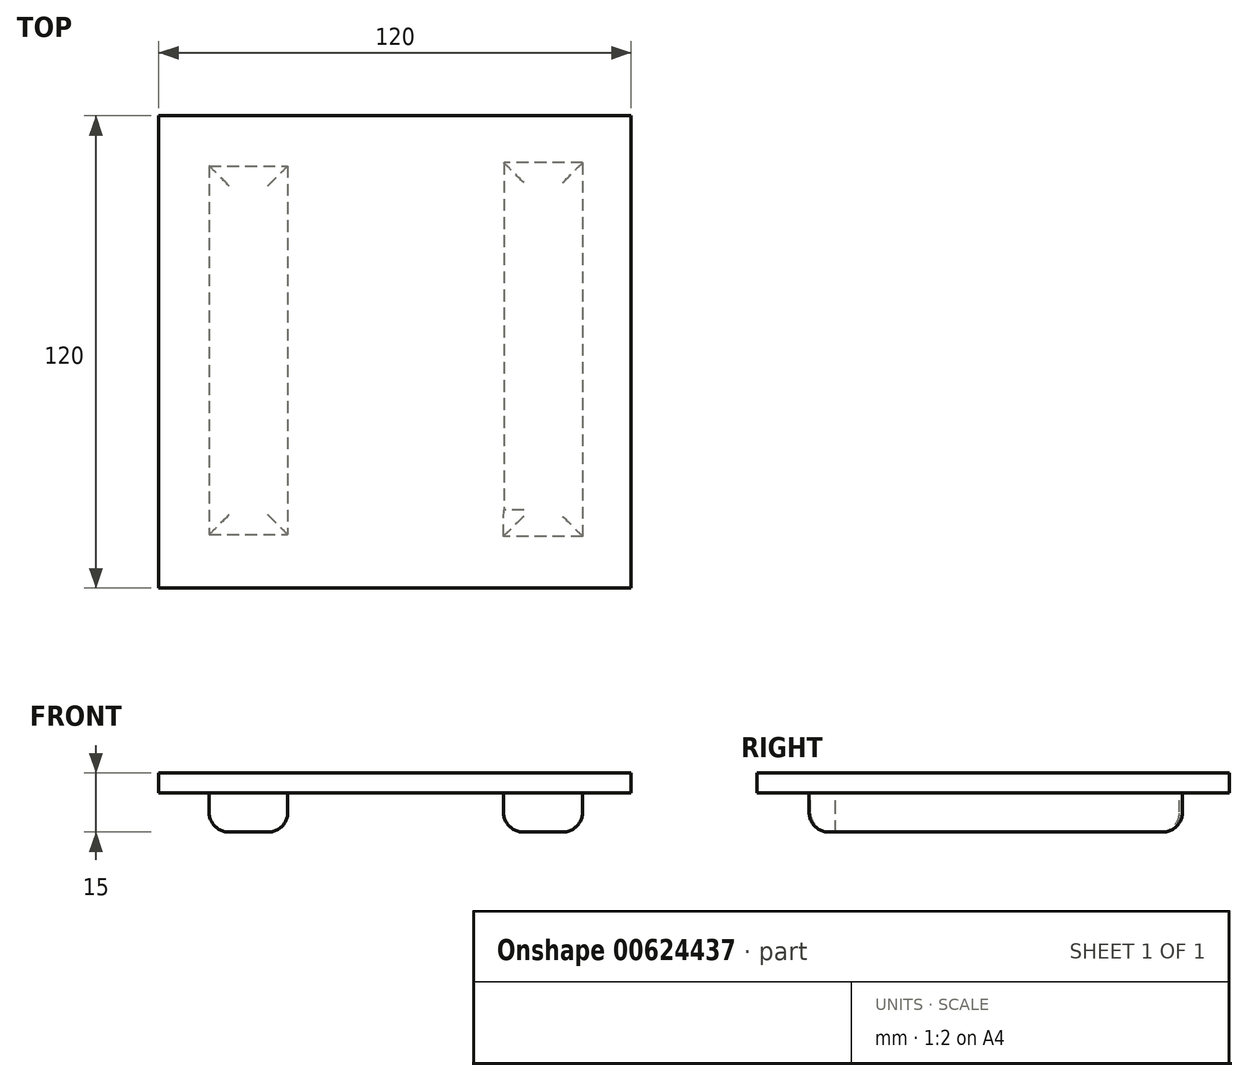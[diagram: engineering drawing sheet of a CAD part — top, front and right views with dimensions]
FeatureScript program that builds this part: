
annotation { "Feature Type Name" : "Feature", "Feature Type Description" : "" }
export const myFeature = defineFeature(function(context is Context, id is Id, definition is map)
    precondition{}
    {
        {
            var Q0;
            Q0=qCreatedBy(makeId("Top.planeOp"),FACE);
            var sketch = newSketch(context, id + "F0", { "sketchPlane" : qUnion([Q0])});
            skLineSegment(sketch, "E0.bottom", {"start": v(60, -60) * mm, "end": v(-60, -60) * mm});
            skLineSegment(sketch, "E0.top", {"start": v(60, 60) * mm, "end": v(-60, 60) * mm});
            skLineSegment(sketch, "E0.left", {"start": v(60, -60) * mm, "end": v(60, 60) * mm});
            skLineSegment(sketch, "E0.right", {"start": v(-60, -60) * mm, "end": v(-60, 60) * mm});
            skPoint(sketch, "E0.middle", {"position": v(0, 0) * mm});
            skSolve(sketch);
        }
        {
            var Q0;
            Q0 = qSketchRegion(id + "F0", true);
            extrude(context, id + "F1", {"entities" : qUnion([Q0]), "depth" : 5 * mm, "offsetDistance" : 25.4 * mm});
        }
        {
            var Q0;
            Q0=qCreatedBy(makeId("Top.planeOp"),FACE);
            var sketch = newSketch(context, id + "F2", { "sketchPlane" : qUnion([Q0])});
            skLineSegment(sketch, "E1.left", {"start": v(-47.24, 47.28) * mm, "end": v(-47.24, -46.44) * mm});
            skLineSegment(sketch, "E2.right", {"start": v(47.65, 48.07) * mm, "end": v(47.65, -46.83) * mm});
            skLineSegment(sketch, "E3", {"start": v(-47.24, 47.28) * mm, "end": v(-27.24, 47.28) * mm});
            skLineSegment(sketch, "E4", {"start": v(-47.24, -46.44) * mm, "end": v(-27.24, -46.44) * mm});
            skLineSegment(sketch, "E5", {"start": v(-27.24, 47.28) * mm, "end": v(-27.24, -46.44) * mm});
            skLineSegment(sketch, "E6", {"start": v(47.65, 48.07) * mm, "end": v(27.65, 48.07) * mm});
            skLineSegment(sketch, "E7", {"start": v(27.65, 48.07) * mm, "end": v(27.65, -45) * mm});
            skLineSegment(sketch, "E8", {"start": v(47.65, -46.83) * mm, "end": v(27.54, -46.83) * mm});
            skLineSegment(sketch, "E9", {"start": v(27.54, -46.83) * mm, "end": v(27.65, -40.15) * mm});
            skSolve(sketch);
        }
        {
            var Q0;
            Q0 = qSketchRegion(id + "F2", true);
            extrude(context, id + "F3", {"entities" : qUnion([Q0]), "operationType" : NewBodyOperationType.ADD, "oppositeDirection" : true, "depth" : 10 * mm, "offsetDistance" : 25.4 * mm});
        }
        {
            var Q0;
            Q0=makeQuery(id+"F3.opExtrude","CAP_EDGE",EDGE,{"disambiguationData":[OSD([sQuery(id+"F2.wireOp",EDGE,"E7")])],"isStart":false});
            var Q1;
            Q1=makeQuery(id+"F3.opExtrude","CAP_EDGE",EDGE,{"disambiguationData":[OSD([sQuery(id+"F2.wireOp",EDGE,"E9")])],"isStart":false});
            var Q2;
            Q2=makeQuery(id+"F3.opExtrude","CAP_EDGE",EDGE,{"disambiguationData":[OSD([sQuery(id+"F2.wireOp",EDGE,"E2.right")])],"isStart":false});
            var Q3;
            Q3=makeQuery(id+"F3.opExtrude","CAP_EDGE",EDGE,{"disambiguationData":[OSD([sQuery(id+"F2.wireOp",EDGE,"E6")])],"isStart":false});
            var Q4;
            Q4=makeQuery(id+"F3.opExtrude","CAP_FACE",FACE,{"disambiguationData":[OSD([sQuery(id+"F2.wireOp",EDGE,"E2.right"),sQuery(id+"F2.wireOp",EDGE,"E6"),sQuery(id+"F2.wireOp",EDGE,"E7"),sQuery(id+"F2.wireOp",EDGE,"E8"),sQuery(id+"F2.wireOp",EDGE,"E9")])],"isStart":false});
            var Q5;
            Q5=makeQuery(id+"F3.opExtrude","CAP_EDGE",EDGE,{"disambiguationData":[OSD([sQuery(id+"F2.wireOp",EDGE,"E5")])],"isStart":false});
            var Q6;
            Q6=makeQuery(id+"F3.opExtrude","CAP_EDGE",EDGE,{"disambiguationData":[OSD([sQuery(id+"F2.wireOp",EDGE,"E1.left")])],"isStart":false});
            var Q7;
            Q7=makeQuery(id+"F3.opExtrude","CAP_EDGE",EDGE,{"disambiguationData":[OSD([sQuery(id+"F2.wireOp",EDGE,"E3")])],"isStart":false});
            var Q8;
            Q8=makeQuery(id+"F3.opExtrude","CAP_EDGE",EDGE,{"disambiguationData":[OSD([sQuery(id+"F2.wireOp",EDGE,"E4")])],"isStart":false});
            fillet(context, id + "F4", {"entities" : qUnion([Q0, Q1, Q2, Q3, Q4, Q5, Q6, Q7, Q8]), "radius" : 5.08 * mm, "tangentPropagation" : true, "allowEdgeOverflow" : false});
        }
    });
